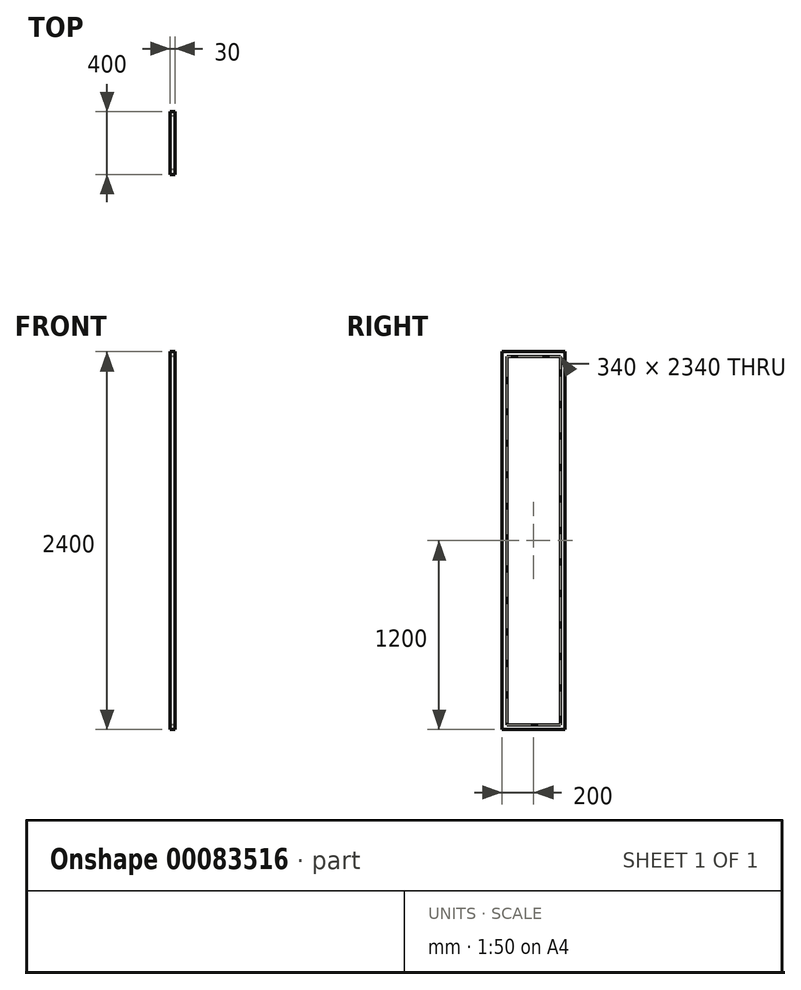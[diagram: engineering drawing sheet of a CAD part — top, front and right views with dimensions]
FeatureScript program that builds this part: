
annotation { "Feature Type Name" : "Feature", "Feature Type Description" : "" }
export const myFeature = defineFeature(function(context is Context, id is Id, definition is map)
    precondition{}
    {
        {
            var Q0;
            Q0=qCreatedBy(makeId("Right.planeOp"),FACE);
            var sketch = newSketch(context, id + "F0", { "sketchPlane" : qUnion([Q0])});
            skLineSegment(sketch, "E0.bottom", {"start": v(-200, 1200) * mm, "end": v(200, 1200) * mm});
            skLineSegment(sketch, "E0.top", {"start": v(-200, -1200) * mm, "end": v(200, -1200) * mm});
            skLineSegment(sketch, "E0.left", {"start": v(-200, 1200) * mm, "end": v(-200, -1200) * mm});
            skLineSegment(sketch, "E0.right", {"start": v(200, 1200) * mm, "end": v(200, -1200) * mm});
            skPoint(sketch, "E0.middle", {"position": v(0, 0) * mm});
            skLineSegment(sketch, "E1.0", {"start": v(-170, 1170) * mm, "end": v(170, 1170) * mm});
            skLineSegment(sketch, "E1.1", {"start": v(-170, 1170) * mm, "end": v(-170, -1170) * mm});
            skLineSegment(sketch, "E1.2", {"start": v(-170, -1170) * mm, "end": v(170, -1170) * mm});
            skLineSegment(sketch, "E1.3", {"start": v(170, 1170) * mm, "end": v(170, -1170) * mm});
            skSolve(sketch);
        }
        {
            var Q0;
            Q0=makeQuery(id+"F0.imprint","IMPRINT",FACE,{"disambiguationData":[TD([[makeQuery(id+"F0.imprint","IMPRINT",EDGE,{"derivedFrom":sQuery(id+"F0.wireOp",EDGE,"E0.bottom")}),-1.0]])]});
            extrude(context, id + "F1", {"entities" : qUnion([Q0]), "depth" : 30 * mm});
        }
    });
